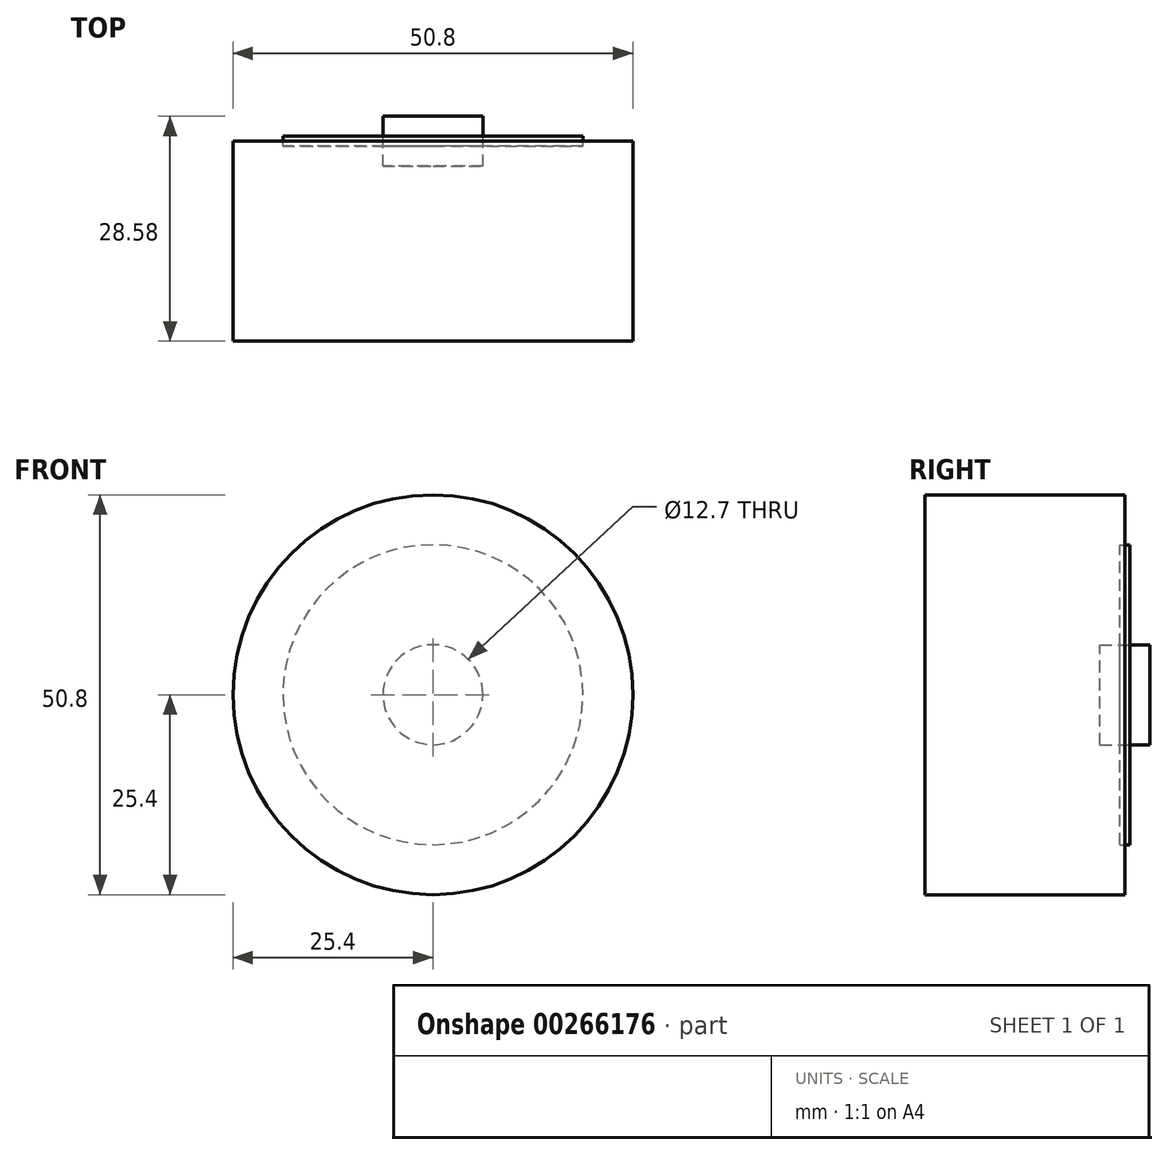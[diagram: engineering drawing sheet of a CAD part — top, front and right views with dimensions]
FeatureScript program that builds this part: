
annotation { "Feature Type Name" : "Feature", "Feature Type Description" : "" }
export const myFeature = defineFeature(function(context is Context, id is Id, definition is map)
    precondition{}
    {
        {
            var Q0;
            Q0=qCreatedBy(makeId("Front.planeOp"),FACE);
            var sketch = newSketch(context, id + "F0", { "sketchPlane" : qUnion([Q0])});
            skCircle(sketch, "E0", {"center": v(0, 0) * mm, "radius": 25.4 * mm});
            skCircle(sketch, "E1", {"center": v(0, 0) * mm, "radius": 19.05 * mm});
            skCircle(sketch, "E2", {"center": v(0, 0) * mm, "radius": 6.35 * mm});
            skSolve(sketch);
        }
        {
            var Q0;
            Q0=makeQuery(id+"F0.imprint","IMPRINT",FACE,{"disambiguationData":[TD([[makeQuery(id+"F0.imprint","IMPRINT",EDGE,{"derivedFrom":sQuery(id+"F0.wireOp",EDGE,"E0")}),1.0]])]});
            var Q1;
            Q1=makeQuery(id+"F0.imprint","IMPRINT",FACE,{"disambiguationData":[TD([[makeQuery(id+"F0.imprint","IMPRINT",EDGE,{"derivedFrom":sQuery(id+"F0.wireOp",EDGE,"E1")}),1.0]])]});
            var Q2;
            Q2=makeQuery(id+"F0.imprint","IMPRINT",FACE,{"disambiguationData":[TD([[makeQuery(id+"F0.imprint","IMPRINT",EDGE,{"derivedFrom":sQuery(id+"F0.wireOp",EDGE,"E2")}),1.0]])]});
            extrude(context, id + "F1", {"entities" : qUnion([Q0, Q1, Q2]), "depth" : 25.4 * mm});
        }
        {
            var Q0;
            Q0=makeQuery(id+"F0.imprint","IMPRINT",FACE,{"disambiguationData":[TD([[makeQuery(id+"F0.imprint","IMPRINT",EDGE,{"derivedFrom":sQuery(id+"F0.wireOp",EDGE,"E1")}),1.0]])]});
            extrude(context, id + "F2", {"entities" : qUnion([Q0]), "endBound" : BoundingType.SYMMETRIC, "depth" : 1.27 * mm});
        }
        {
            var Q0;
            Q0=makeQuery(id+"F0.imprint","IMPRINT",FACE,{"disambiguationData":[TD([[makeQuery(id+"F0.imprint","IMPRINT",EDGE,{"derivedFrom":sQuery(id+"F0.wireOp",EDGE,"E2")}),1.0]])]});
            extrude(context, id + "F3", {"entities" : qUnion([Q0]), "endBound" : BoundingType.SYMMETRIC, "depth" : 6.35 * mm});
        }
    });
